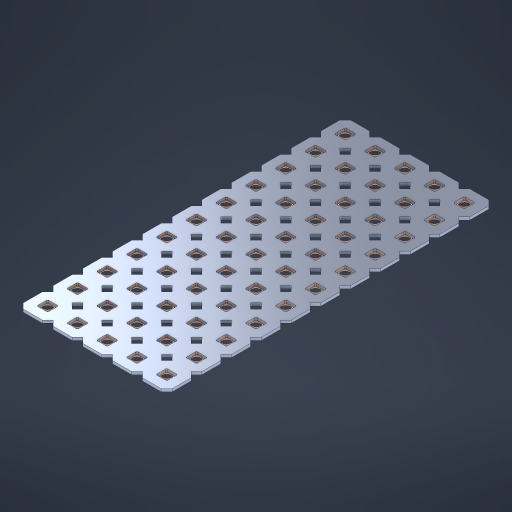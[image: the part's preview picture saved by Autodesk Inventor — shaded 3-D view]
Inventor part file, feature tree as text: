
AUTODESK INVENTOR PART (.ipt)
format: ipt  version: 2023 (Build 270158000, 158)  size: 901,632 bytes
history: native  units: in
note: dims shown in document units (in); Inventor stores cm internally (conversion verified against a paired STEP export)
features: other x56, extrude x54, sketch x2, pattern_linear x1
ambient origin geometry x8: Origin, YZ Plane, XZ Plane, XY Plane, X Axis, Y Axis, Z Axis, Center Point
bodies: Solid1 (feature_tree), Body (feature_tree)
feature tree (113):
  pattern_linear  "Rectangular Pattern1"  Spacing1=0.09in  [1 undecoded]
  sketch  "Sketch1"  dims[d1=0.5in]
  sketch  "Sketch2"  dims[d2=0.182in d3=0.09in d4=0.09in d5=0.09in d6=0.09in d7=0.09in d8=0.09in d9=0.09in d10=0.09in d11=0.02in d13=0.0in d14=0.172in d15=0.0625in d16=0.0in d19=0.5in d22=0.5in]
  other  "Srf1"
  other  "Srf126"
  other  "Srf127"
  other  "Srf128"
  other  "Srf129"
  other  "Srf130"
  other  "Srf131"
  other  "Srf250"
  other  "Srf251"
  other  "Srf252"
  other  "Srf253"
  other  "Srf268"
  other  "Srf269"
  other  "Srf270"
  other  "Srf271"
  other  "Srf272"
  other  "Srf273"
  other  "Srf274"
  other  "Srf275"
  other  "Srf276"
  other  "Srf277"
  other  "Srf278"
  other  "Srf293"
  other  "Srf294"
  other  "Srf295"
  other  "Srf296"
  other  "Srf297"
  other  "Srf298"
  other  "Srf299"
  other  "Srf300"
  other  "Srf301"
  other  "Srf302"
  other  "Srf303"
  other  "Srf318"
  other  "Srf319"
  other  "Srf320"
  other  "Srf321"
  other  "Srf322"
  other  "Srf323"
  other  "Srf324"
  other  "Srf325"
  other  "Srf326"
  other  "Srf327"
  other  "Srf328"
  other  "Srf343"
  other  "Srf344"
  other  "Srf345"
  other  "Srf346"
  other  "Srf347"
  other  "Srf348"
  other  "Srf349"
  other  "Srf350"
  other  "Srf351"
  other  "Srf352"
  other  "Srf353"
  other  "Circle"
  extrude  "ExtrusionSrf126"  Depth=0.09in
  extrude  "ExtrusionSrf127"  Depth=0.09in
  extrude  "ExtrusionSrf128"  Depth=0.09in
  extrude  "ExtrusionSrf129"  Depth=0.09in
  extrude  "ExtrusionSrf130"  Depth=0.09in
  extrude  "ExtrusionSrf131"  Depth=0.09in
  extrude  "ExtrusionSrf250"  Depth=0.09in
  extrude  "ExtrusionSrf251"  Depth=0.02in
  extrude  "ExtrusionSrf252"  TaperAngle=0.0deg  [1 undecoded]
  extrude  "ExtrusionSrf253"  Depth=0.5in
  extrude  "ExtrusionSrf268"  Depth=0.5in TaperAngle=0.0deg
  extrude  "ExtrusionSrf269"  Depth=0.5in
  extrude  "ExtrusionSrf270"  Depth=0.5in
  extrude  "ExtrusionSrf271"  [1 undecoded]
  extrude  "ExtrusionSrf272"  [1 undecoded]
  extrude  "ExtrusionSrf273"  [1 undecoded]
  extrude  "ExtrusionSrf274"  [1 undecoded]
  extrude  "ExtrusionSrf275"  [1 undecoded]
  extrude  "ExtrusionSrf276"  [1 undecoded]
  extrude  "ExtrusionSrf277"  [1 undecoded]
  extrude  "ExtrusionSrf278"  [1 undecoded]
  extrude  "ExtrusionSrf293"  [1 undecoded]
  extrude  "ExtrusionSrf294"  [1 undecoded]
  extrude  "ExtrusionSrf295"  [1 undecoded]
  extrude  "ExtrusionSrf296"  [1 undecoded]
  extrude  "ExtrusionSrf297"  [1 undecoded]
  extrude  "ExtrusionSrf298"  [1 undecoded]
  extrude  "ExtrusionSrf299"  [1 undecoded]
  extrude  "ExtrusionSrf300"  [1 undecoded]
  extrude  "ExtrusionSrf301"  [1 undecoded]
  extrude  "ExtrusionSrf302"  [1 undecoded]
  extrude  "ExtrusionSrf303"  [1 undecoded]
  extrude  "ExtrusionSrf318"  [1 undecoded]
  extrude  "ExtrusionSrf319"  [1 undecoded]
  extrude  "ExtrusionSrf320"  [1 undecoded]
  extrude  "ExtrusionSrf321"  [1 undecoded]
  extrude  "ExtrusionSrf322"  [1 undecoded]
  extrude  "ExtrusionSrf323"  [1 undecoded]
  extrude  "ExtrusionSrf324"  [1 undecoded]
  extrude  "ExtrusionSrf325"  [1 undecoded]
  extrude  "ExtrusionSrf326"  [1 undecoded]
  extrude  "ExtrusionSrf327"  [1 undecoded]
  extrude  "ExtrusionSrf328"  [1 undecoded]
  extrude  "ExtrusionSrf343"  [1 undecoded]
  extrude  "ExtrusionSrf344"  [1 undecoded]
  extrude  "ExtrusionSrf345"  [1 undecoded]
  extrude  "ExtrusionSrf346"  [1 undecoded]
  extrude  "ExtrusionSrf347"  [1 undecoded]
  extrude  "ExtrusionSrf348"  [1 undecoded]
  extrude  "ExtrusionSrf349"  [1 undecoded]
  extrude  "ExtrusionSrf350"  [1 undecoded]
  extrude  "ExtrusionSrf351"  [1 undecoded]
  extrude  "ExtrusionSrf352"  [1 undecoded]
  extrude  "ExtrusionSrf353"  [1 undecoded]
note: 43 required parameter values undecoded (feature->parameter linkage not recoverable at this tier; creation-order binding heuristic only, values carry confidence <= 0.55)
